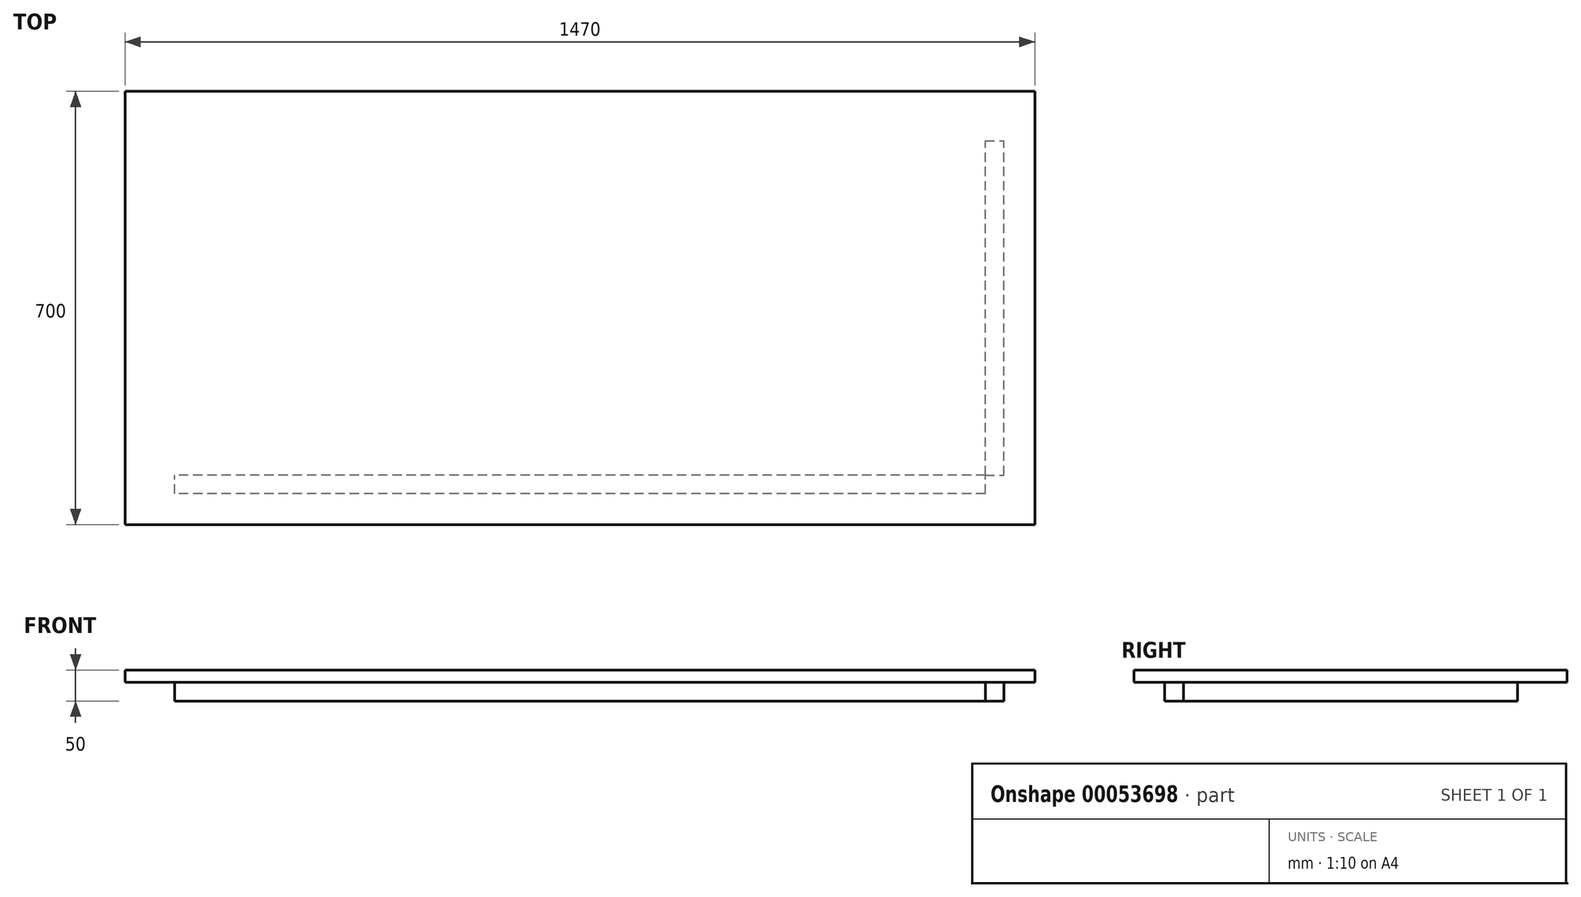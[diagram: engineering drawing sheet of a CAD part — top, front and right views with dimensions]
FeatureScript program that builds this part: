
annotation { "Feature Type Name" : "Feature", "Feature Type Description" : "" }
export const myFeature = defineFeature(function(context is Context, id is Id, definition is map)
    precondition{}
    {
        {
            var Q0;
            Q0=qCreatedBy(makeId("Top.planeOp"),FACE);
            var sketch = newSketch(context, id + "F0", { "sketchPlane" : qUnion([Q0])});
            skLineSegment(sketch, "E0.rect.bottom", {"start": v(735, -350) * mm, "end": v(-735, -350) * mm});
            skLineSegment(sketch, "E0.rect.top", {"start": v(735, 350) * mm, "end": v(-735, 350) * mm});
            skLineSegment(sketch, "E0.rect.left", {"start": v(735, -350) * mm, "end": v(735, 350) * mm});
            skLineSegment(sketch, "E0.rect.right", {"start": v(-735, -350) * mm, "end": v(-735, 350) * mm});
            skPoint(sketch, "E0.rect.middle", {"position": v(0, 0) * mm});
            skSolve(sketch);
        }
        {
            var Q0;
            Q0=qSketchRegion(id+"F0",true);
            extrude(context, id + "F1", {"entities" : qUnion([Q0]), "endBound" : BoundingType.SYMMETRIC, "depth" : 20 * mm});
        }
        {
            var Q0;
            Q0=qCreatedBy(makeId("Front.planeOp"),FACE);
            var sketch = newSketch(context, id + "F2", { "sketchPlane" : qUnion([Q0])});
            skLineSegment(sketch, "E1.bottom", {"start": v(655, -10) * mm, "end": v(685, -10) * mm});
            skLineSegment(sketch, "E1.top", {"start": v(655, -40) * mm, "end": v(685, -40) * mm});
            skLineSegment(sketch, "E1.left", {"start": v(655, -10) * mm, "end": v(655, -40) * mm});
            skLineSegment(sketch, "E1.right", {"start": v(685, -10) * mm, "end": v(685, -40) * mm});
            skSolve(sketch);
        }
        {
            var Q0;
            Q0 = qSketchRegion(id + "F2", true);
            extrude(context, id + "F3", {"entities" : qUnion([Q0]), "endBound" : BoundingType.SYMMETRIC, "depth" : 540 * mm});
        }
        {
            var Q0;
            Q0=qCreatedBy(makeId("Right.planeOp"),FACE);
            var sketch = newSketch(context, id + "F4", { "sketchPlane" : qUnion([Q0])});
            skLineSegment(sketch, "E2.bottom", {"start": v(-300, -10) * mm, "end": v(-270, -10) * mm});
            skLineSegment(sketch, "E2.top", {"start": v(-300, -40) * mm, "end": v(-270, -40) * mm});
            skLineSegment(sketch, "E2.left", {"start": v(-300, -10) * mm, "end": v(-300, -40) * mm});
            skLineSegment(sketch, "E2.right", {"start": v(-270, -10) * mm, "end": v(-270, -40) * mm});
            skSolve(sketch);
        }
        {
            var Q0;
            Q0 = qSketchRegion(id + "F4", true);
            extrude(context, id + "F5", {"entities" : qUnion([Q0]), "endBound" : BoundingType.SYMMETRIC, "depth" : 1310 * mm});
        }
    });
